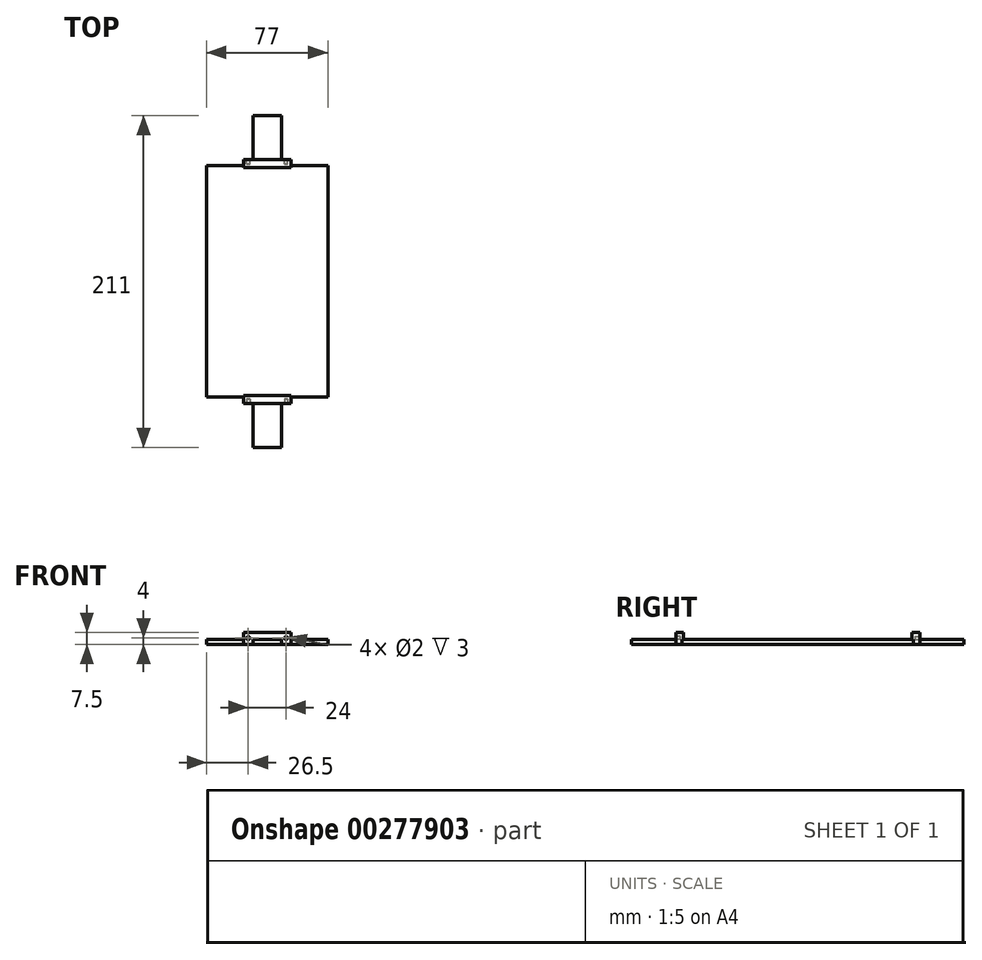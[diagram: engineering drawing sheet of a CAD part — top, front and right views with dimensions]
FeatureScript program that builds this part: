
annotation { "Feature Type Name" : "Feature", "Feature Type Description" : "" }
export const myFeature = defineFeature(function(context is Context, id is Id, definition is map)
    precondition{}
    {
        {
            var Q0;
            Q0=qCreatedBy(makeId("Top.planeOp"),FACE);
            var sketch = newSketch(context, id + "F0", { "sketchPlane" : qUnion([Q0])});
            skLineSegment(sketch, "E0", {"start": v(0, 0) * mm, "end": v(0, 105.5) * mm, "construction": true});
            skLineSegment(sketch, "E1", {"start": v(-9, 73.5) * mm, "end": v(-9, 105.5) * mm});
            skLineSegment(sketch, "E2", {"start": v(-9, 105.5) * mm, "end": v(0, 105.5) * mm});
            skLineSegment(sketch, "E3", {"start": v(-9, 73.5) * mm, "end": v(-38.5, 73.5) * mm});
            skLineSegment(sketch, "E4", {"start": v(-38.5, 73.5) * mm, "end": v(-38.5, -73.5) * mm});
            skLineSegment(sketch, "E5", {"start": v(-38.5, -73.5) * mm, "end": v(-9, -73.5) * mm});
            skLineSegment(sketch, "E6", {"start": v(-9, -73.5) * mm, "end": v(-9, -105.5) * mm});
            skLineSegment(sketch, "E7", {"start": v(-9, -105.5) * mm, "end": v(0, -105.5) * mm});
            skLineSegment(sketch, "E8", {"start": v(-38.5, 0) * mm, "end": v(0, 0) * mm, "construction": true});
            skLineSegment(sketch, "E9.MirrorCS", {"start": v(9, 105.5) * mm, "end": v(0, 105.5) * mm});
            skLineSegment(sketch, "E10.MirrorCS", {"start": v(9, 73.5) * mm, "end": v(9, 105.5) * mm});
            skLineSegment(sketch, "E11.MirrorCS", {"start": v(9, 73.5) * mm, "end": v(38.5, 73.5) * mm});
            skLineSegment(sketch, "E12.MirrorCS", {"start": v(38.5, 73.5) * mm, "end": v(38.5, -73.5) * mm});
            skLineSegment(sketch, "E13.MirrorCS", {"start": v(38.5, -73.5) * mm, "end": v(9, -73.5) * mm});
            skLineSegment(sketch, "E14.MirrorCS", {"start": v(9, -73.5) * mm, "end": v(9, -105.5) * mm});
            skLineSegment(sketch, "E15.MirrorCS", {"start": v(9, -105.5) * mm, "end": v(0, -105.5) * mm});
            skSolve(sketch);
        }
        {
            var Q0;
            Q0 = qSketchRegion(id + "F0", true);
            extrude(context, id + "F1", {"entities" : qUnion([Q0]), "depth" : 3 * mm});
        }
        {
            var Q0;
            Q0=makeQuery(id+"F1.opExtrude","CAP_FACE",FACE,{"disambiguationData":[OSD([sQuery(id+"F0.wireOp",EDGE,"E1"),sQuery(id+"F0.wireOp",EDGE,"E2"),sQuery(id+"F0.wireOp",EDGE,"E3"),sQuery(id+"F0.wireOp",EDGE,"E4"),sQuery(id+"F0.wireOp",EDGE,"E5"),sQuery(id+"F0.wireOp",EDGE,"E6"),sQuery(id+"F0.wireOp",EDGE,"E7"),sQuery(id+"F0.wireOp",EDGE,"E9.MirrorCS"),sQuery(id+"F0.wireOp",EDGE,"E10.MirrorCS"),sQuery(id+"F0.wireOp",EDGE,"E11.MirrorCS"),sQuery(id+"F0.wireOp",EDGE,"E12.MirrorCS"),sQuery(id+"F0.wireOp",EDGE,"E13.MirrorCS"),sQuery(id+"F0.wireOp",EDGE,"E14.MirrorCS"),sQuery(id+"F0.wireOp",EDGE,"E15.MirrorCS")])],"isStart":false});
            var sketch = newSketch(context, id + "F2", { "sketchPlane" : qUnion([Q0])});
            skLineSegment(sketch, "E16.top", {"start": v(-15, 77.5) * mm, "end": v(15, 77.5) * mm});
            skLineSegment(sketch, "E16.right", {"start": v(15, 72.5) * mm, "end": v(15, 77.5) * mm});
            skLineSegment(sketch, "E17", {"start": v(0, 77.5) * mm, "end": v(0, 105.5) * mm, "construction": true});
            skPoint(sketch, "E17.startSnap0", {"position": v(0, 77.5) * mm});
            skLineSegment(sketch, "E18", {"start": v(-15, 77.5) * mm, "end": v(-15, 72.5) * mm});
            skLineSegment(sketch, "E19", {"start": v(-15, 72.5) * mm, "end": v(15, 72.5) * mm});
            skLineSegment(sketch, "E20", {"start": v(0, 0) * mm, "end": v(38.5, 0) * mm, "construction": true});
            skLineSegment(sketch, "E21.MirrorCS", {"start": v(-15, -77.5) * mm, "end": v(15, -77.5) * mm});
            skLineSegment(sketch, "E22.MirrorCS", {"start": v(-15, -77.5) * mm, "end": v(-15, -72.5) * mm});
            skLineSegment(sketch, "E23.MirrorCS", {"start": v(-15, -72.5) * mm, "end": v(15, -72.5) * mm});
            skLineSegment(sketch, "E24.MirrorCS", {"start": v(15, -72.5) * mm, "end": v(15, -77.5) * mm});
            skSolve(sketch);
        }
        {
            var Q0;
            Q0 = qSketchRegion(id + "F2", true);
            var Q1;
            Q1=makeQuery(id+"F1.opExtrude","CAP_FACE",FACE,{"disambiguationData":[OSD([sQuery(id+"F0.wireOp",EDGE,"E1"),sQuery(id+"F0.wireOp",EDGE,"E2"),sQuery(id+"F0.wireOp",EDGE,"E3"),sQuery(id+"F0.wireOp",EDGE,"E4"),sQuery(id+"F0.wireOp",EDGE,"E5"),sQuery(id+"F0.wireOp",EDGE,"E6"),sQuery(id+"F0.wireOp",EDGE,"E7"),sQuery(id+"F0.wireOp",EDGE,"E9.MirrorCS"),sQuery(id+"F0.wireOp",EDGE,"E10.MirrorCS"),sQuery(id+"F0.wireOp",EDGE,"E11.MirrorCS"),sQuery(id+"F0.wireOp",EDGE,"E12.MirrorCS"),sQuery(id+"F0.wireOp",EDGE,"E13.MirrorCS"),sQuery(id+"F0.wireOp",EDGE,"E14.MirrorCS"),sQuery(id+"F0.wireOp",EDGE,"E15.MirrorCS")])],"isStart":true});
            extrude(context, id + "F3", {"entities" : qUnion([Q0]), "operationType" : NewBodyOperationType.ADD, "depth" : 4.5 * mm, "hasSecondDirection" : true, "secondDirectionBound" : BoundingType.UP_TO_SURFACE, "secondDirectionOppositeDirection" : true, "secondDirectionBoundEntityFace" : qUnion([Q1]), "secondDirectionDepth" : 25 * mm});
        }
        {
            var Q0;
            Q0=makeQuery(id+"F3.opExtrude","SWEPT_FACE",FACE,{"disambiguationData":[OSD([sQuery(id+"F2.wireOp",EDGE,"E16.top")])]});
            var sketch = newSketch(context, id + "F4", { "sketchPlane" : qUnion([Q0])});
            skCircle(sketch, "E25", {"center": v(-12, 4) * mm, "radius": 1 * mm});
            skLineSegment(sketch, "E26", {"start": v(0, 0) * mm, "end": v(0, 7.5) * mm, "construction": true});
            skCircle(sketch, "E27.MirrorC", {"center": v(12, 4) * mm, "radius": 1 * mm});
            skSolve(sketch);
        }
        {
            var Q0;
            Q0 = qSketchRegion(id + "F4", true);
            extrude(context, id + "F5", {"entities" : qUnion([Q0]), "operationType" : NewBodyOperationType.REMOVE, "oppositeDirection" : true, "depth" : 3 * mm});
        }
        {
            var Q0;
            Q0=makeQuery(id+"F3.opExtrude","SWEPT_FACE",FACE,{"disambiguationData":[OSD([sQuery(id+"F2.wireOp",EDGE,"E21.MirrorCS")])]});
            var sketch = newSketch(context, id + "F6", { "sketchPlane" : qUnion([Q0])});
            skCircle(sketch, "E28.0", {"center": v(12, 4) * mm, "radius": 1 * mm});
            skCircle(sketch, "E29.0", {"center": v(-12, 4) * mm, "radius": 1 * mm});
            skSolve(sketch);
        }
        {
            var Q0;
            Q0 = qSketchRegion(id + "F6", true);
            extrude(context, id + "F7", {"entities" : qUnion([Q0]), "operationType" : NewBodyOperationType.REMOVE, "oppositeDirection" : true, "depth" : 3 * mm});
        }
    });
